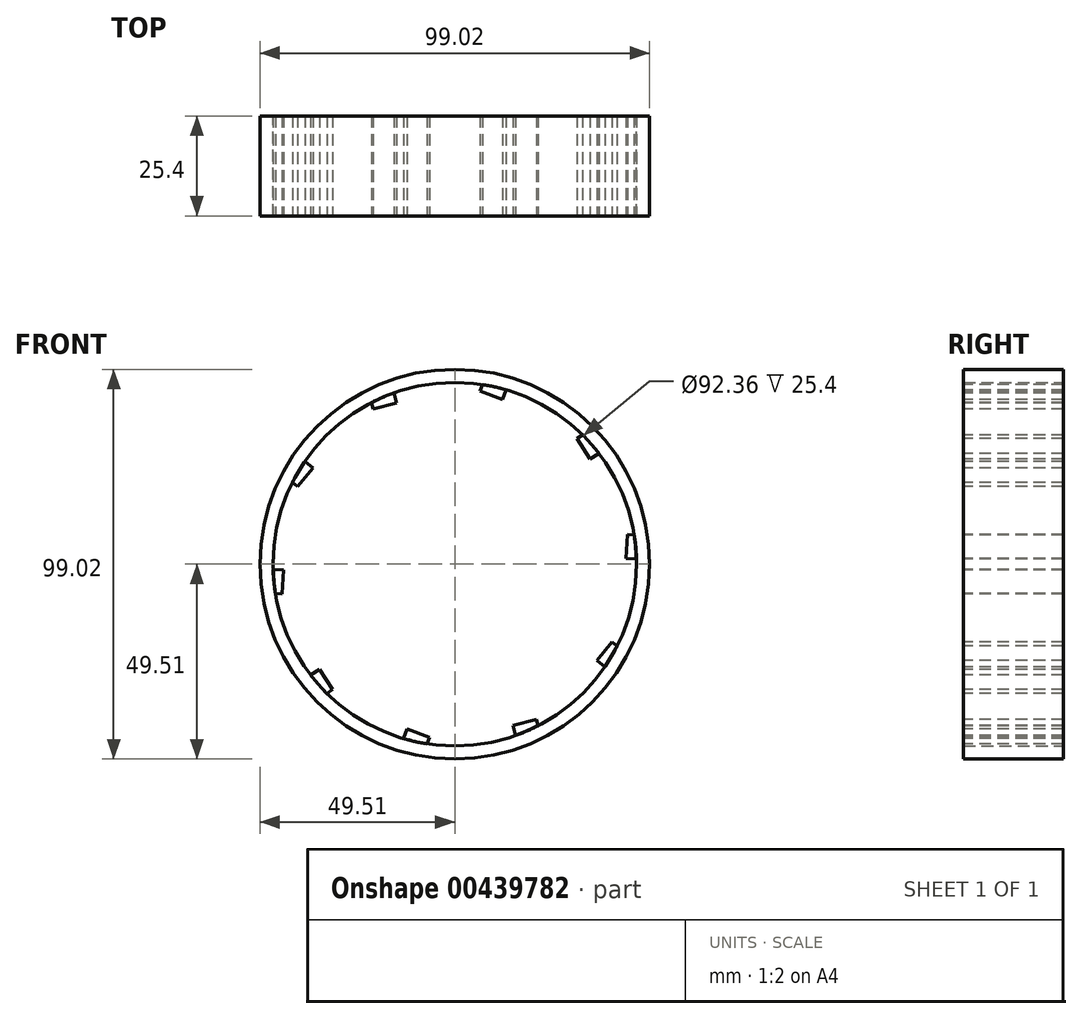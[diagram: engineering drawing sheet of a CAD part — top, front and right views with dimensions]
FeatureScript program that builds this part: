
annotation { "Feature Type Name" : "Feature", "Feature Type Description" : "" }
export const myFeature = defineFeature(function(context is Context, id is Id, definition is map)
    precondition{}
    {
        {
            var Q0;
            Q0=qCreatedBy(makeId("Front.planeOp"),FACE);
            var sketch = newSketch(context, id + "F0", { "sketchPlane" : qUnion([Q0])});
            skCircle(sketch, "E0", {"center": v(0, 0) * mm, "radius": 49.51 * mm});
            skCircle(sketch, "E1", {"center": v(0, 0) * mm, "radius": 46.18 * mm});
            skSolve(sketch);
        }
        {
            var Q0;
            Q0=makeQuery(id+"F0.imprint","IMPRINT",FACE,{"disambiguationData":[TD([[makeQuery(id+"F0.imprint","IMPRINT",EDGE,{"derivedFrom":sQuery(id+"F0.wireOp",EDGE,"E0")}),1.0]])]});
            extrude(context, id + "F1", {"entities" : qUnion([Q0]), "depth" : 25.4 * mm});
        }
        {
            var Q0;
            Q0=makeQuery(id+"F1.opExtrude","CAP_FACE",FACE,{"disambiguationData":[OSD([sQuery(id+"F0.wireOp",EDGE,"E0"),sQuery(id+"F0.wireOp",EDGE,"E1")])],"isStart":false});
            var sketch = newSketch(context, id + "F2", { "sketchPlane" : qUnion([Q0])});
            skLineSegment(sketch, "E2", {"start": v(-38.1, 26.1) * mm, "end": v(-36.06, 24.44) * mm});
            skLineSegment(sketch, "E3", {"start": v(-36.06, 24.44) * mm, "end": v(-39.92, 19.7) * mm});
            skLineSegment(sketch, "E4", {"start": v(-39.92, 19.7) * mm, "end": v(-41.24, 20.77) * mm});
            skSolve(sketch);
        }
        {
            var Q0;
            {var subQ0=sQuery(id+"F2.wireOp",EDGE,"E2");Q0=makeQuery(id+"F2.imprint","IMPRINT",FACE,{"disambiguationData":[TD([[makeQuery(id+"F2.imprint","IMPRINT",EDGE,{"derivedFrom":subQ0}),-1.0]])]});}
            extrude(context, id + "F3", {"entities" : qUnion([Q0]), "oppositeDirection" : true, "depth" : 25.4 * mm});
        }
        {
            var Q0;
            Q0=makeQuery(id+"F3.opExtrude","SWEPT_BODY",BODY,{"disambiguationData":[OSD([sQuery(id+"F0.wireOp",EDGE,"E1"),sQuery(id+"F2.wireOp",EDGE,"E2"),sQuery(id+"F2.wireOp",EDGE,"E3"),sQuery(id+"F2.wireOp",EDGE,"E4")])]});
            var Q1;
            Q1=makeQuery(id+"F1.opExtrude","SWEPT_FACE",FACE,{"disambiguationData":[OSD([sQuery(id+"F0.wireOp",EDGE,"E1")])]});
            circularPattern(context, id + "F4", {"entities" : qUnion([Q0]), "axis" : qUnion([Q1]), "angle" : 360 * degree, "instanceCount" : 10, "equalSpace" : true});
        }
    });
